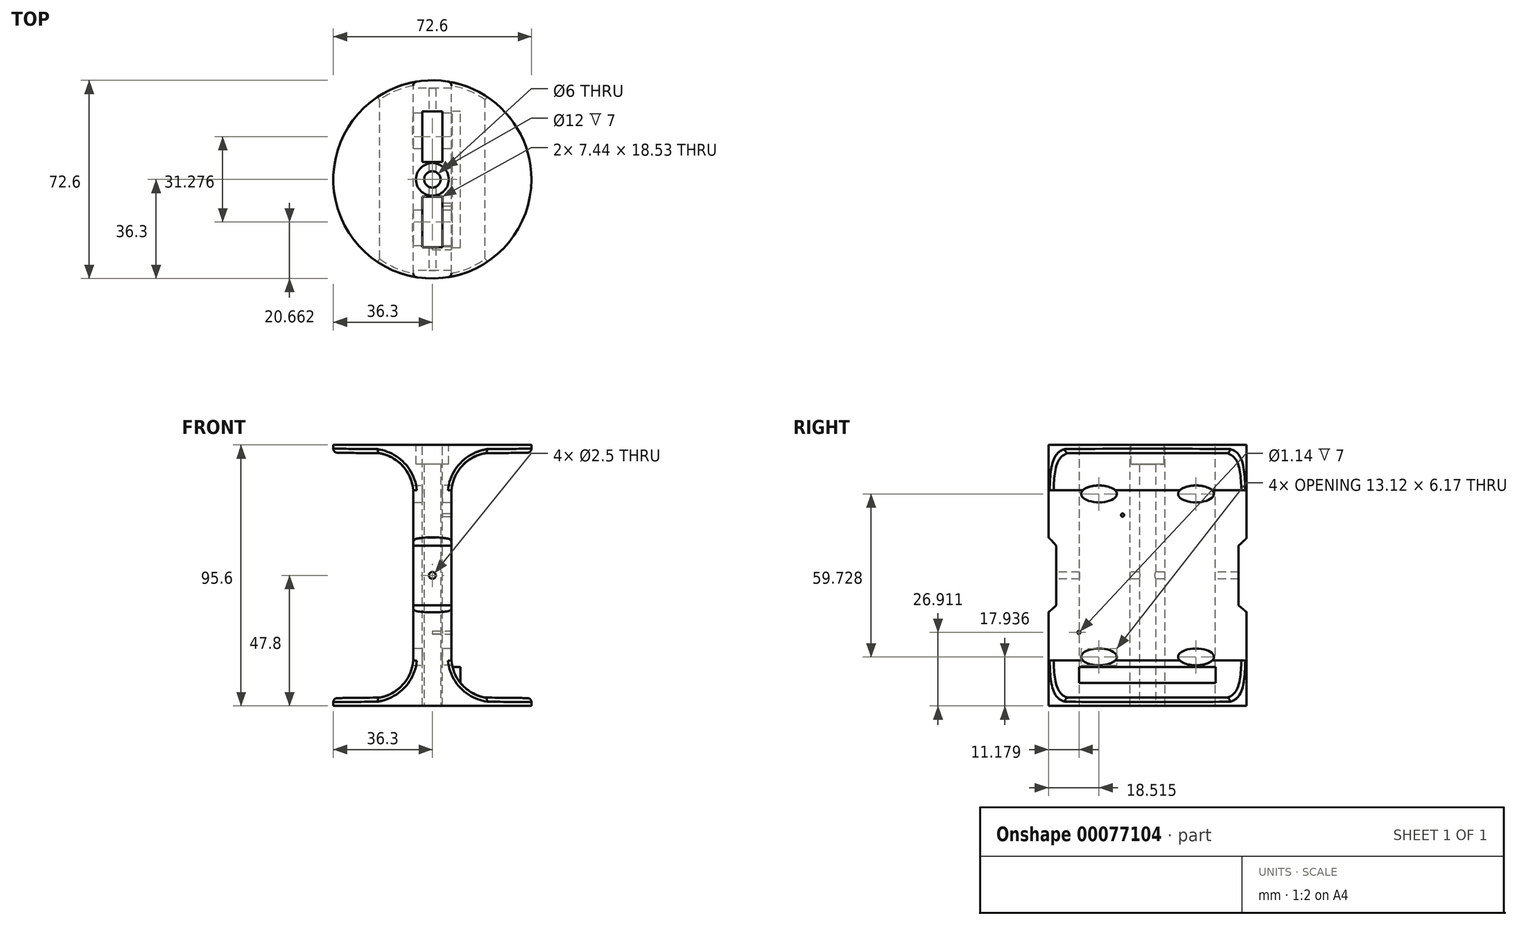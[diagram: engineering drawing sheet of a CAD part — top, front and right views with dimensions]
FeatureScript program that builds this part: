
annotation { "Feature Type Name" : "Feature", "Feature Type Description" : "" }
export const myFeature = defineFeature(function(context is Context, id is Id, definition is map)
    precondition{}
    {
        {
            var Q0;
            Q0=qCreatedBy(makeId("Top.planeOp"),FACE);
            var sketch = newSketch(context, id + "F0", { "sketchPlane" : qUnion([Q0])});
            skCircle(sketch, "E0", {"center": v(0, 0) * mm, "radius": 36.3 * mm});
            skCircle(sketch, "E1", {"center": v(0, 0) * mm, "radius": 3 * mm});
            skSolve(sketch);
        }
        {
            var Q0;
            Q0=makeQuery(id+"F0.imprint","IMPRINT",FACE,{"disambiguationData":[TD([[makeQuery(id+"F0.imprint","IMPRINT",EDGE,{"derivedFrom":sQuery(id+"F0.wireOp",EDGE,"E0")}),1.0]])]});
            extrude(context, id + "F1", {"entities" : qUnion([Q0]), "depth" : 95.6 * mm, "offsetDistance" : 25 * mm, "symmetric" : true});
        }
        {
            var Q0;
            Q0=qCreatedBy(makeId("Front.planeOp"),FACE);
            var sketch = newSketch(context, id + "F2", { "sketchPlane" : qUnion([Q0])});
            skArc(sketch, "E2", {"start": v(-7, 31.17) * mm, "mid": v(-11.47, 40.72) * mm, "end": v(-21.1, 44.98) * mm});
            skPoint(sketch, "E2.first.point", {"position": v(-26.4, 44.33) * mm});
            skPoint(sketch, "E2.second.point", {"position": v(-13.67, 17.5) * mm});
            skPoint(sketch, "E2.third.point", {"position": v(-11.88, 18.9) * mm});
            skLineSegment(sketch, "E3", {"start": v(-33.8, 39.21) * mm, "end": v(-33.85, 39.2) * mm});
            skLineSegment(sketch, "E4", {"start": v(-7, 31.17) * mm, "end": v(-7, 0) * mm});
            skLineSegment(sketch, "E5", {"start": v(-29.95, 0) * mm, "end": v(-7, 0) * mm, "construction": true});
            skLineSegment(sketch, "E6.MirrorCS", {"start": v(-7, -31.17) * mm, "end": v(-7, 0) * mm});
            skPoint(sketch, "E7.orphan", {"position": v(-22.37, 15) * mm});
            skPoint(sketch, "E8.orphan", {"position": v(-22.37, -15) * mm});
            skPoint(sketch, "E9.orphan", {"position": v(-13.67, -17.5) * mm});
            skLineSegment(sketch, "E10.MirrorCS", {"start": v(-33.8, -39.21) * mm, "end": v(-33.85, -39.2) * mm});
            skPoint(sketch, "E11.MirrorCS.end.orphan", {"position": v(-29.95, 0) * mm});
            skPoint(sketch, "E11.MirrorCS.start.orphan", {"position": v(-29.95, -17.3) * mm});
            skPoint(sketch, "E12.MirrorCS.center.orphan", {"position": v(-21.96, -30) * mm});
            skPoint(sketch, "E12.MirrorCS.end.orphan", {"position": v(-21.1, -44.98) * mm});
            skLineSegment(sketch, "E13", {"start": v(-19.34, 44.77) * mm, "end": v(-37.9, 44.98) * mm});
            skLineSegment(sketch, "E14.MirrorCS", {"start": v(-19.34, -44.77) * mm, "end": v(-37.9, -44.98) * mm});
            skArc(sketch, "E15.MirrorCS", {"start": v(-7, -31.17) * mm, "mid": v(-11.47, -40.72) * mm, "end": v(-21.1, -44.98) * mm});
            skPoint(sketch, "E16.start.orphan", {"position": v(-29.95, 17.3) * mm});
            skLineSegment(sketch, "E17", {"start": v(-37.9, 44.98) * mm, "end": v(-37.9, -44.98) * mm});
            skPoint(sketch, "E18.end.orphan", {"position": v(-36.94, 29.1) * mm});
            skPoint(sketch, "E19.MirrorCS.end.orphan", {"position": v(-36.94, -29.1) * mm});
            skPoint(sketch, "E20.MirrorCS.start.orphan", {"position": v(-33.28, -39.85) * mm});
            skPoint(sketch, "E21.MirrorCS.start.orphan", {"position": v(-33.85, -39.2) * mm});
            skPoint(sketch, "E22.end.orphan", {"position": v(-33.28, 39.85) * mm});
            skSolve(sketch);
        }
        {
            var Q0;
            {var subQ0=sQuery(id+"F2.wireOp",EDGE,"E2");Q0=makeQuery(id+"F2.imprint","IMPRINT",FACE,{"disambiguationData":[TD([[makeQuery(id+"F2.imprint","IMPRINT",EDGE,{"derivedFrom":subQ0}),1.0]])]});}
            extrude(context, id + "F3", {"entities" : qUnion([Q0]), "depth" : 100 * mm, "offsetDistance" : 25 * mm, "symmetric" : true});
        }
        {
            var Q0;
            Q0=makeQuery(id+"F3.opExtrude","SWEPT_BODY",BODY,{"disambiguationData":[OSD([sQuery(id+"F2.wireOp",EDGE,"E2"),sQuery(id+"F2.wireOp",EDGE,"2f42745c-d287-4b53-8fb5-9bfce6a12ec3"),sQuery(id+"F2.wireOp",EDGE,"bZKIiQnf-FhRn-fojp-zsQL-YmqztP06htcK")])]});
            var Q1;
            Q1=qCreatedBy(makeId("Right.planeOp"),FACE);
            mirror(context, id + "F4", {"operationType" : NewBodyOperationType.REMOVE, "entities" : qUnion([Q0]), "mirrorPlane" : qUnion([Q1])});
        }
        {
            var Q0;
            Q0=makeQuery(id+"F3.opExtrude","SWEPT_BODY",BODY,{"disambiguationData":[OSD([sQuery(id+"F2.wireOp",EDGE,"E2"),sQuery(id+"F2.wireOp",EDGE,"2f42745c-d287-4b53-8fb5-9bfce6a12ec3"),sQuery(id+"F2.wireOp",EDGE,"bZKIiQnf-FhRn-fojp-zsQL-YmqztP06htcK")])]});
            var Q1;
            Q1=makeQuery(id+"F1.opExtrude","SWEPT_BODY",BODY,{"disambiguationData":[OSD([sQuery(id+"F0.wireOp",EDGE,"E0"),sQuery(id+"F0.wireOp",EDGE,"E1")])]});
            booleanBodies(context, id + "F5", {"operationType" : BooleanOperationType.SUBTRACTION, "tools" : qUnion([Q0]), "targets" : qUnion([Q1])});
        }
        {
            var Q0;
            Q0=makeQuery(id+"F1.opExtrude","CAP_FACE",FACE,{"disambiguationData":[OSD([sQuery(id+"F0.wireOp",EDGE,"E0"),sQuery(id+"F0.wireOp",EDGE,"E1")])],"isStart":false});
            var sketch = newSketch(context, id + "F6", { "sketchPlane" : qUnion([Q0])});
            skLineSegment(sketch, "E23.bottom", {"start": v(-4.66, 24.9) * mm, "end": v(3.72, 24.9) * mm});
            skLineSegment(sketch, "E23.top", {"start": v(-4.66, 6.37) * mm, "end": v(3.72, 6.37) * mm});
            skLineSegment(sketch, "E23.left", {"start": v(-4.66, 24.9) * mm, "end": v(-4.66, 6.37) * mm});
            skLineSegment(sketch, "E23.right", {"start": v(3.72, 24.9) * mm, "end": v(3.72, 6.37) * mm});
            skLineSegment(sketch, "E24", {"start": v(0, 63.63) * mm, "end": v(0, -56.2) * mm, "construction": true});
            skLineSegment(sketch, "E25.MirrorCS", {"start": v(4.66, 24.9) * mm, "end": v(-3.72, 24.9) * mm});
            skLineSegment(sketch, "E26.MirrorCS", {"start": v(4.66, 24.9) * mm, "end": v(4.66, 6.37) * mm});
            skLineSegment(sketch, "E27.MirrorCS", {"start": v(4.66, 6.37) * mm, "end": v(-3.72, 6.37) * mm});
            skLineSegment(sketch, "E28.MirrorCS", {"start": v(-3.72, 24.9) * mm, "end": v(-3.72, 6.37) * mm});
            skSolve(sketch);
        }
        {
            var Q0;
            {var subQ0=sQuery(id+"F6.wireOp",EDGE,"E23.right");Q0=makeQuery(id+"F6.imprint","IMPRINT",FACE,{"disambiguationData":[TD([[makeQuery(id+"F6.imprint","IMPRINT",EDGE,{"derivedFrom":subQ0}),-1.0]])]});}
            var Q1;
            Q1=makeQuery(id+"F1.opExtrude","CAP_FACE",FACE,{"disambiguationData":[OSD([sQuery(id+"F0.wireOp",EDGE,"E0"),sQuery(id+"F0.wireOp",EDGE,"E1")])],"isStart":true});
            extrude(context, id + "F7", {"entities" : qUnion([Q0]), "endBound" : BoundingType.UP_TO_SURFACE, "oppositeDirection" : true, "depth" : 25 * mm, "endBoundEntityFace" : qUnion([Q1]), "offsetDistance" : 25 * mm});
        }
        {
            var Q0;
            Q0=makeQuery(id+"F7.opExtrude","SWEPT_BODY",BODY,{"disambiguationData":[OSD([sQuery(id+"F6.wireOp",EDGE,"E23.right"),sQuery(id+"F6.wireOp",EDGE,"E28.MirrorCS"),sQuery(id+"F6.wireOp",EDGE,"E23.top"),sQuery(id+"F6.wireOp",EDGE,"E23.bottom")])]});
            var Q1;
            Q1=qCreatedBy(makeId("Front.planeOp"),FACE);
            mirror(context, id + "F8", {"operationType" : NewBodyOperationType.REMOVE, "entities" : qUnion([Q0]), "mirrorPlane" : qUnion([Q1])});
        }
        {
            var Q0;
            Q0=makeQuery(id+"F7.opExtrude","SWEPT_BODY",BODY,{"disambiguationData":[OSD([sQuery(id+"F6.wireOp",EDGE,"E23.right"),sQuery(id+"F6.wireOp",EDGE,"E28.MirrorCS"),sQuery(id+"F6.wireOp",EDGE,"E23.top"),sQuery(id+"F6.wireOp",EDGE,"E23.bottom")])]});
            var Q1;
            Q1=makeQuery(id+"F1.opExtrude","SWEPT_BODY",BODY,{"disambiguationData":[OSD([sQuery(id+"F0.wireOp",EDGE,"E0"),sQuery(id+"F0.wireOp",EDGE,"E1")])]});
            booleanBodies(context, id + "F9", {"operationType" : BooleanOperationType.SUBTRACTION, "tools" : qUnion([Q0]), "targets" : qUnion([Q1])});
        }
        {
            var Q0;
            Q0=qCreatedBy(makeId("Right.planeOp"),FACE);
            var sketch = newSketch(context, id + "F10", { "sketchPlane" : qUnion([Q0])});
            skLineSegment(sketch, "E29.left", {"start": v(-41.37, 0) * mm, "end": v(-41.37, 10.94) * mm});
            skLineSegment(sketch, "E29.right", {"start": v(-33.38, 0) * mm, "end": v(-33.38, 10.94) * mm});
            skLineSegment(sketch, "E30.MirrorCS", {"start": v(-41.37, 0) * mm, "end": v(-41.37, -9.04) * mm});
            skLineSegment(sketch, "E31.MirrorCS", {"start": v(-33.38, 0) * mm, "end": v(-33.38, -9.04) * mm});
            skLineSegment(sketch, "E32.MirrorCS", {"start": v(-41.37, 0) * mm, "end": v(-41.37, -10.94) * mm});
            skLineSegment(sketch, "E33.MirrorCS", {"start": v(-33.38, 0) * mm, "end": v(-33.38, -10.94) * mm});
            skLineSegment(sketch, "E34.MirrorCS", {"start": v(33.38, 0) * mm, "end": v(33.38, 10.94) * mm});
            skLineSegment(sketch, "E35.MirrorCS", {"start": v(41.37, 0) * mm, "end": v(41.37, -10.94) * mm});
            skLineSegment(sketch, "E36.MirrorCS", {"start": v(41.37, 0) * mm, "end": v(41.37, 10.94) * mm});
            skLineSegment(sketch, "E37.MirrorCS", {"start": v(33.38, 0) * mm, "end": v(33.38, -10.94) * mm});
            skLineSegment(sketch, "E38", {"start": v(-33.38, 10.94) * mm, "end": v(-41.37, 19.28) * mm});
            skLineSegment(sketch, "E39", {"start": v(-41.37, 19.28) * mm, "end": v(-41.37, 10.94) * mm});
            skLineSegment(sketch, "E40", {"start": v(-33.38, -10.94) * mm, "end": v(-41.37, -18.03) * mm});
            skLineSegment(sketch, "E41", {"start": v(-41.37, -18.03) * mm, "end": v(-41.37, -10.94) * mm});
            skLineSegment(sketch, "E42", {"start": v(33.38, 10.94) * mm, "end": v(41.37, 18.2) * mm});
            skLineSegment(sketch, "E43", {"start": v(41.37, 18.2) * mm, "end": v(41.37, 10.94) * mm});
            skLineSegment(sketch, "E44", {"start": v(33.38, -10.94) * mm, "end": v(41.37, -17.85) * mm});
            skLineSegment(sketch, "E45", {"start": v(41.37, -17.85) * mm, "end": v(41.37, -10.94) * mm});
            skPoint(sketch, "E46.MirrorCS.start.orphan", {"position": v(41.37, -10.94) * mm});
            skSolve(sketch);
        }
        {
            var Q0;
            {var subQ4=sQuery(id+"F10.wireOp",EDGE,"E29.left");Q0=makeQuery(id+"F10.imprint","IMPRINT",FACE,{"disambiguationData":[TD([[makeQuery(id+"F10.imprint","IMPRINT",EDGE,{"derivedFrom":subQ4}),-1.0]])]});}
            var Q1;
            Q1=makeQuery(id+"F10.imprint","IMPRINT",FACE,{"disambiguationData":[TD([[makeQuery(id+"F10.imprint","IMPRINT",EDGE,{"derivedFrom":sQuery(id+"F10.wireOp",EDGE,"E34.MirrorCS")}),-1.0]])]});
            extrude(context, id + "F11", {"entities" : qUnion([Q0, Q1]), "operationType" : NewBodyOperationType.REMOVE, "depth" : 25 * mm, "offsetDistance" : 25 * mm, "symmetric" : true});
        }
        {
            var Q0;
            Q0=makeQuery(id+"F11.boolean.opBoolean","COPY",FACE,{"derivedFrom":makeQuery(id+"F11.opExtrude","SWEPT_FACE",FACE,{"disambiguationData":[OSD([sQuery(id+"F10.wireOp",EDGE,"E29.right"),sQuery(id+"F10.wireOp",EDGE,"E33.MirrorCS")])]})});
            var sketch = newSketch(context, id + "F12", { "sketchPlane" : qUnion([Q0])});
            skCircle(sketch, "E47", {"center": v(0, 0) * mm, "radius": 1.25 * mm});
            skSolve(sketch);
        }
        {
            var Q0;
            Q0=makeQuery(id+"F12.imprint","IMPRINT",FACE,{"disambiguationData":[TD([[makeQuery(id+"F12.imprint","IMPRINT",EDGE,{"derivedFrom":sQuery(id+"F12.wireOp",EDGE,"E47")}),1.0]])]});
            extrude(context, id + "F13", {"entities" : qUnion([Q0]), "operationType" : NewBodyOperationType.REMOVE, "oppositeDirection" : true, "depth" : 100 * mm, "offsetDistance" : 25 * mm});
        }
        {
            var Q0;
            Q0=makeQuery(id+"F4.boolean.opBoolean","COPY",FACE,{"derivedFrom":makeQuery(id+"F4.opPattern","COPY",FACE,{"derivedFrom":makeQuery(id+"F3.opExtrude","SWEPT_FACE",FACE,{"disambiguationData":[OSD([sQuery(id+"F2.wireOp",EDGE,"E4"),sQuery(id+"F2.wireOp",EDGE,"E6.MirrorCS")])]}),"instanceName":"1"})});
            var sketch = newSketch(context, id + "F14", { "sketchPlane" : qUnion([Q0])});
            skLineSegment(sketch, "E48.bottom", {"start": v(-26.56, 23.2) * mm, "end": v(-7.51, 23.2) * mm});
            skLineSegment(sketch, "E48.top", {"start": v(-26.56, -22.54) * mm, "end": v(-7.51, -22.54) * mm});
            skLineSegment(sketch, "E48.left", {"start": v(-26.56, 23.2) * mm, "end": v(-26.56, -22.54) * mm});
            skLineSegment(sketch, "E48.right", {"start": v(-7.51, 23.2) * mm, "end": v(-7.51, -22.54) * mm});
            skSolve(sketch);
        }
        {
            var Q0;
            Q0=qCreatedBy(makeId("Right.planeOp"),FACE);
            var sketch = newSketch(context, id + "F15", { "sketchPlane" : qUnion([Q0])});
            skEllipse(sketch, "E49", {"center": v(-17.79, 29.86) * mm, "majorRadius": 6.56 * mm, "minorRadius": 3.09 * mm, "majorAxis": v(1, 0)});
            skEllipse(sketch, "E50.MirrorC", {"center": v(-17.79, -29.86) * mm, "majorRadius": 6.56 * mm, "minorRadius": 3.09 * mm, "majorAxis": v(1, 0)});
            skEllipse(sketch, "E51.MirrorC", {"center": v(17.79, -29.86) * mm, "majorRadius": 6.56 * mm, "minorRadius": 3.09 * mm, "majorAxis": v(-1, 0)});
            skEllipse(sketch, "E52.MirrorC", {"center": v(17.79, 29.86) * mm, "majorRadius": 6.56 * mm, "minorRadius": 3.09 * mm, "majorAxis": v(-1, 0)});
            skSolve(sketch);
        }
        {
            var Q0;
            Q0=makeQuery(id+"F15.imprint","IMPRINT",FACE,{"disambiguationData":[TD([[makeQuery(id+"F15.imprint","IMPRINT",EDGE,{"derivedFrom":sQuery(id+"F15.wireOp",EDGE,"E49")}),1.0]])]});
            var Q1;
            Q1=makeQuery(id+"F15.imprint","IMPRINT",FACE,{"disambiguationData":[TD([[makeQuery(id+"F15.imprint","IMPRINT",EDGE,{"derivedFrom":sQuery(id+"F15.wireOp",EDGE,"E50.MirrorC")}),1.0]])]});
            var Q2;
            Q2=makeQuery(id+"F15.imprint","IMPRINT",FACE,{"disambiguationData":[TD([[makeQuery(id+"F15.imprint","IMPRINT",EDGE,{"derivedFrom":sQuery(id+"F15.wireOp",EDGE,"E52.MirrorC")}),1.0]])]});
            var Q3;
            Q3=makeQuery(id+"F15.imprint","IMPRINT",FACE,{"disambiguationData":[TD([[makeQuery(id+"F15.imprint","IMPRINT",EDGE,{"derivedFrom":sQuery(id+"F15.wireOp",EDGE,"E51.MirrorC")}),1.0]])]});
            extrude(context, id + "F16", {"entities" : qUnion([Q0, Q1, Q2, Q3]), "operationType" : NewBodyOperationType.REMOVE, "depth" : 30 * mm, "offsetDistance" : 25 * mm, "symmetric" : true});
        }
        {
            var Q0;
            Q0=makeQuery(id+"F14.imprint","IMPRINT",FACE,{"disambiguationData":[TD([[makeQuery(id+"F14.imprint","IMPRINT",EDGE,{"derivedFrom":sQuery(id+"F14.wireOp",EDGE,"E48.bottom")}),1.0]])]});
            var sketch = newSketch(context, id + "F17", { "sketchPlane" : qUnion([Q0])});
            skCircle(sketch, "E53", {"center": v(6.54, 23.06) * mm, "radius": 0.57 * mm});
            skCircle(sketch, "E54", {"center": v(23.04, 23.06) * mm, "radius": 0.57 * mm});
            skLineSegment(sketch, "E55", {"start": v(6.54, 23.06) * mm, "end": v(7.1, 23.06) * mm, "construction": true});
            skCircle(sketch, "E56", {"center": v(6.54, -22.66) * mm, "radius": 0.57 * mm});
            skLineSegment(sketch, "E57", {"start": v(6.54, 23.06) * mm, "end": v(6.54, 22.49) * mm, "construction": true});
            skLineSegment(sketch, "E58", {"start": v(6.54, -22.66) * mm, "end": v(7.1, -22.66) * mm, "construction": true});
            skCircle(sketch, "E59", {"center": v(23.04, -22.66) * mm, "radius": 0.57 * mm});
            skCircle(sketch, "E60", {"center": v(-25.12, 22.11) * mm, "radius": 0.57 * mm});
            skCircle(sketch, "E61", {"center": v(-9.12, 22.11) * mm, "radius": 0.57 * mm});
            skLineSegment(sketch, "E62", {"start": v(-25.12, 22.11) * mm, "end": v(-24.55, 22.11) * mm, "construction": true});
            skCircle(sketch, "E63", {"center": v(-25.12, -20.89) * mm, "radius": 0.57 * mm});
            skLineSegment(sketch, "E64", {"start": v(-25.12, -20.89) * mm, "end": v(-24.55, -20.89) * mm, "construction": true});
            skCircle(sketch, "E65", {"center": v(-8.62, -20.89) * mm, "radius": 0.57 * mm});
            skLineSegment(sketch, "E66", {"start": v(-25.12, 22.11) * mm, "end": v(-25.12, 21.54) * mm, "construction": true});
            skLineSegment(sketch, "E67", {"start": v(-9.12, 22.11) * mm, "end": v(-9.32, 21.58) * mm});
            skLineSegment(sketch, "E68.trimOffspring", {"start": v(-24.92, -20.35) * mm, "end": v(-25.12, -20.89) * mm});
            skLineSegment(sketch, "E69.trimOffspring", {"start": v(6.54, -22.1) * mm, "end": v(6.54, -60.18) * mm, "construction": true});
            skLineSegment(sketch, "E70.trimOffspring", {"start": v(22.47, 23.06) * mm, "end": v(25.23, 23.06) * mm, "construction": true});
            skLineSegment(sketch, "E71.trimOffspring", {"start": v(22.47, -22.66) * mm, "end": v(26.07, -22.66) * mm, "construction": true});
            skLineSegment(sketch, "E72.trimOffspring", {"start": v(-9.2, -20.89) * mm, "end": v(-8.05, -20.89) * mm, "construction": true});
            skLineSegment(sketch, "E73.trimOffspring", {"start": v(-25.12, -20.32) * mm, "end": v(-25.12, -23.48) * mm, "construction": true});
            skLineSegment(sketch, "E74.trimOffspring", {"start": v(-9.69, 22.11) * mm, "end": v(-8.55, 22.11) * mm, "construction": true});
            skSolve(sketch);
        }
        {
            var Q0;
            Q0=qCreatedBy(makeId("Front.planeOp"),FACE);
            var sketch = newSketch(context, id + "F18", { "sketchPlane" : qUnion([Q0])});
            skLineSegment(sketch, "E75.bottom", {"start": v(6.24, -33.56) * mm, "end": v(10.28, -33.56) * mm});
            skLineSegment(sketch, "E75.top", {"start": v(6.24, -40.66) * mm, "end": v(10.28, -40.66) * mm});
            skLineSegment(sketch, "E75.left", {"start": v(6.24, -33.56) * mm, "end": v(6.24, -40.66) * mm});
            skLineSegment(sketch, "E75.right", {"start": v(10.28, -33.56) * mm, "end": v(10.28, -40.66) * mm});
            skSolve(sketch);
        }
        {
            var Q0;
            Q0=makeQuery(id+"F18.imprint","IMPRINT",FACE,{"disambiguationData":[TD([[makeQuery(id+"F18.imprint","IMPRINT",EDGE,{"derivedFrom":sQuery(id+"F18.wireOp",EDGE,"E75.bottom")}),-1.0]])]});
            extrude(context, id + "F19", {"entities" : qUnion([Q0]), "operationType" : NewBodyOperationType.ADD, "depth" : 50 * mm, "offsetDistance" : 25 * mm, "symmetric" : true});
        }
        {
            var Q0;
            Q0=makeQuery(id+"F17.imprint","IMPRINT",FACE,{"disambiguationData":[TD([[makeQuery(id+"F17.imprint","IMPRINT",EDGE,{"derivedFrom":sQuery(id+"F17.wireOp",EDGE,"E61")}),1.0]])]});
            extrude(context, id + "F20", {"entities" : qUnion([Q0]), "operationType" : NewBodyOperationType.REMOVE, "oppositeDirection" : true, "depth" : 5 * mm, "offsetDistance" : 25 * mm});
        }
        {
            var Q0;
            Q0=makeQuery(id+"F17.imprint","IMPRINT",FACE,{"disambiguationData":[TD([[makeQuery(id+"F17.imprint","IMPRINT",EDGE,{"derivedFrom":sQuery(id+"F17.wireOp",EDGE,"E63")}),1.0]])]});
            extrude(context, id + "F21", {"entities" : qUnion([Q0]), "operationType" : NewBodyOperationType.REMOVE, "oppositeDirection" : true, "depth" : 7 * mm, "offsetDistance" : 25 * mm});
        }
        {
            var Q0;
            Q0=makeQuery(id+"F4.boolean.opBoolean","INTERSECT",EDGE,{"disambiguationData":[OD(1.0)],"derivedFrom":[makeQuery(id+"F1.opExtrude","SWEPT_FACE",FACE,{"disambiguationData":[OSD([sQuery(id+"F0.wireOp",EDGE,"E0")])]}),makeQuery(id+"F4.opPattern","COPY",FACE,{"derivedFrom":makeQuery(id+"F3.opExtrude","SWEPT_FACE",FACE,{"disambiguationData":[OSD([sQuery(id+"F2.wireOp",EDGE,"E2")])]}),"instanceName":"1"})]});
            var Q1;
            Q1=makeQuery(id+"F4.boolean.opBoolean","INTERSECT",EDGE,{"derivedFrom":[makeQuery(id+"F1.opExtrude","SWEPT_FACE",FACE,{"disambiguationData":[OSD([sQuery(id+"F0.wireOp",EDGE,"E0")])]}),makeQuery(id+"F4.opPattern","COPY",FACE,{"derivedFrom":makeQuery(id+"F3.opExtrude","SWEPT_FACE",FACE,{"disambiguationData":[OSD([sQuery(id+"F2.wireOp",EDGE,"E13")])]}),"instanceName":"1"})]});
            var Q2;
            {var subQ0=makeQuery(id+"F1.opExtrude","SWEPT_FACE",FACE,{"disambiguationData":[OSD([sQuery(id+"F0.wireOp",EDGE,"E0")])]});var subQ1=makeQuery(id+"F4.opPattern","COPY",FACE,{"derivedFrom":makeQuery(id+"F3.opExtrude","SWEPT_FACE",FACE,{"disambiguationData":[OSD([sQuery(id+"F2.wireOp",EDGE,"E4"),sQuery(id+"F2.wireOp",EDGE,"E6.MirrorCS")])]}),"instanceName":"1"});Q2=makeQuery(id+"F11.boolean.opBoolean","SPLIT",EDGE,{"disambiguationData":[TD([makeQuery(id+"F4.boolean.opBoolean","COPY",FACE,{"derivedFrom":makeQuery(id+"F4.opPattern","COPY",FACE,{"derivedFrom":makeQuery(id+"F3.opExtrude","SWEPT_FACE",FACE,{"disambiguationData":[OSD([sQuery(id+"F2.wireOp",EDGE,"E2")])]}),"instanceName":"1"})})])],"derivedFrom":makeQuery(id+"F4.boolean.opBoolean","INTERSECT",EDGE,{"disambiguationData":[OD(1.0)],"derivedFrom":[subQ0,subQ1]})});}
            var Q3;
            Q3=makeQuery(id+"F4.boolean.opBoolean","INTERSECT",EDGE,{"disambiguationData":[OD(0.0)],"derivedFrom":[makeQuery(id+"F1.opExtrude","SWEPT_FACE",FACE,{"disambiguationData":[OSD([sQuery(id+"F0.wireOp",EDGE,"E0")])]}),makeQuery(id+"F4.opPattern","COPY",FACE,{"derivedFrom":makeQuery(id+"F3.opExtrude","SWEPT_FACE",FACE,{"disambiguationData":[OSD([sQuery(id+"F2.wireOp",EDGE,"E2")])]}),"instanceName":"1"})]});
            var Q4;
            {var subQ0=makeQuery(id+"F1.opExtrude","SWEPT_FACE",FACE,{"disambiguationData":[OSD([sQuery(id+"F0.wireOp",EDGE,"E0")])]});var subQ1=makeQuery(id+"F4.opPattern","COPY",FACE,{"derivedFrom":makeQuery(id+"F3.opExtrude","SWEPT_FACE",FACE,{"disambiguationData":[OSD([sQuery(id+"F2.wireOp",EDGE,"E4"),sQuery(id+"F2.wireOp",EDGE,"E6.MirrorCS")])]}),"instanceName":"1"});Q4=makeQuery(id+"F11.boolean.opBoolean","SPLIT",EDGE,{"disambiguationData":[TD([makeQuery(id+"F4.boolean.opBoolean","COPY",FACE,{"derivedFrom":makeQuery(id+"F4.opPattern","COPY",FACE,{"derivedFrom":makeQuery(id+"F3.opExtrude","SWEPT_FACE",FACE,{"disambiguationData":[OSD([sQuery(id+"F2.wireOp",EDGE,"E2")])]}),"instanceName":"1"})})])],"derivedFrom":makeQuery(id+"F4.boolean.opBoolean","INTERSECT",EDGE,{"disambiguationData":[OD(0.0)],"derivedFrom":[subQ0,subQ1]})});}
            var Q5;
            {var subQ0=makeQuery(id+"F1.opExtrude","SWEPT_FACE",FACE,{"disambiguationData":[OSD([sQuery(id+"F0.wireOp",EDGE,"E0")])]});var subQ1=makeQuery(id+"F4.opPattern","COPY",FACE,{"derivedFrom":makeQuery(id+"F3.opExtrude","SWEPT_FACE",FACE,{"disambiguationData":[OSD([sQuery(id+"F2.wireOp",EDGE,"E4"),sQuery(id+"F2.wireOp",EDGE,"E6.MirrorCS")])]}),"instanceName":"1"});Q5=makeQuery(id+"F11.boolean.opBoolean","SPLIT",EDGE,{"disambiguationData":[TD([makeQuery(id+"F4.boolean.opBoolean","COPY",FACE,{"derivedFrom":makeQuery(id+"F4.opPattern","COPY",FACE,{"derivedFrom":makeQuery(id+"F3.opExtrude","SWEPT_FACE",FACE,{"disambiguationData":[OSD([sQuery(id+"F2.wireOp",EDGE,"E15.MirrorCS")])]}),"instanceName":"1"})})])],"derivedFrom":makeQuery(id+"F4.boolean.opBoolean","INTERSECT",EDGE,{"disambiguationData":[OD(0.0)],"derivedFrom":[subQ0,subQ1]})});}
            var Q6;
            Q6=makeQuery(id+"F4.boolean.opBoolean","INTERSECT",EDGE,{"disambiguationData":[OD(0.0)],"derivedFrom":[makeQuery(id+"F1.opExtrude","SWEPT_FACE",FACE,{"disambiguationData":[OSD([sQuery(id+"F0.wireOp",EDGE,"E0")])]}),makeQuery(id+"F4.opPattern","COPY",FACE,{"derivedFrom":makeQuery(id+"F3.opExtrude","SWEPT_FACE",FACE,{"disambiguationData":[OSD([sQuery(id+"F2.wireOp",EDGE,"E15.MirrorCS")])]}),"instanceName":"1"})]});
            var Q7;
            Q7=makeQuery(id+"F4.boolean.opBoolean","INTERSECT",EDGE,{"derivedFrom":[makeQuery(id+"F1.opExtrude","SWEPT_FACE",FACE,{"disambiguationData":[OSD([sQuery(id+"F0.wireOp",EDGE,"E0")])]}),makeQuery(id+"F4.opPattern","COPY",FACE,{"derivedFrom":makeQuery(id+"F3.opExtrude","SWEPT_FACE",FACE,{"disambiguationData":[OSD([sQuery(id+"F2.wireOp",EDGE,"E14.MirrorCS")])]}),"instanceName":"1"})]});
            var Q8;
            Q8=makeQuery(id+"F4.boolean.opBoolean","INTERSECT",EDGE,{"disambiguationData":[OD(1.0)],"derivedFrom":[makeQuery(id+"F1.opExtrude","SWEPT_FACE",FACE,{"disambiguationData":[OSD([sQuery(id+"F0.wireOp",EDGE,"E0")])]}),makeQuery(id+"F4.opPattern","COPY",FACE,{"derivedFrom":makeQuery(id+"F3.opExtrude","SWEPT_FACE",FACE,{"disambiguationData":[OSD([sQuery(id+"F2.wireOp",EDGE,"E15.MirrorCS")])]}),"instanceName":"1"})]});
            var Q9;
            {var subQ0=makeQuery(id+"F1.opExtrude","SWEPT_FACE",FACE,{"disambiguationData":[OSD([sQuery(id+"F0.wireOp",EDGE,"E0")])]});var subQ1=makeQuery(id+"F4.opPattern","COPY",FACE,{"derivedFrom":makeQuery(id+"F3.opExtrude","SWEPT_FACE",FACE,{"disambiguationData":[OSD([sQuery(id+"F2.wireOp",EDGE,"E4"),sQuery(id+"F2.wireOp",EDGE,"E6.MirrorCS")])]}),"instanceName":"1"});Q9=makeQuery(id+"F11.boolean.opBoolean","SPLIT",EDGE,{"disambiguationData":[TD([makeQuery(id+"F4.boolean.opBoolean","COPY",FACE,{"derivedFrom":makeQuery(id+"F4.opPattern","COPY",FACE,{"derivedFrom":makeQuery(id+"F3.opExtrude","SWEPT_FACE",FACE,{"disambiguationData":[OSD([sQuery(id+"F2.wireOp",EDGE,"E15.MirrorCS")])]}),"instanceName":"1"})})])],"derivedFrom":makeQuery(id+"F4.boolean.opBoolean","INTERSECT",EDGE,{"disambiguationData":[OD(1.0)],"derivedFrom":[subQ0,subQ1]})});}
            var Q10;
            Q10=makeQuery(id+"F5.opBoolean","INTERSECT",EDGE,{"disambiguationData":[OD(1.0)],"derivedFrom":[makeQuery(id+"F3.opExtrude","SWEPT_FACE",FACE,{"disambiguationData":[OSD([sQuery(id+"F2.wireOp",EDGE,"E15.MirrorCS")])]}),makeQuery(id+"F1.opExtrude","SWEPT_FACE",FACE,{"disambiguationData":[OSD([sQuery(id+"F0.wireOp",EDGE,"E0")])]})]});
            var Q11;
            Q11=makeQuery(id+"F5.opBoolean","INTERSECT",EDGE,{"derivedFrom":[makeQuery(id+"F3.opExtrude","SWEPT_FACE",FACE,{"disambiguationData":[OSD([sQuery(id+"F2.wireOp",EDGE,"E14.MirrorCS")])]}),makeQuery(id+"F1.opExtrude","SWEPT_FACE",FACE,{"disambiguationData":[OSD([sQuery(id+"F0.wireOp",EDGE,"E0")])]})]});
            var Q12;
            {var subQ0=makeQuery(id+"F1.opExtrude","SWEPT_FACE",FACE,{"disambiguationData":[OSD([sQuery(id+"F0.wireOp",EDGE,"E0")])]});var subQ1=makeQuery(id+"F3.opExtrude","SWEPT_FACE",FACE,{"disambiguationData":[OSD([sQuery(id+"F2.wireOp",EDGE,"E4"),sQuery(id+"F2.wireOp",EDGE,"E6.MirrorCS")])]});Q12=makeQuery(id+"F11.boolean.opBoolean","SPLIT",EDGE,{"disambiguationData":[TD([makeQuery(id+"F5.opBoolean","COPY",FACE,{"derivedFrom":makeQuery(id+"F3.opExtrude","SWEPT_FACE",FACE,{"disambiguationData":[OSD([sQuery(id+"F2.wireOp",EDGE,"E15.MirrorCS")])]})})])],"derivedFrom":makeQuery(id+"F5.opBoolean","INTERSECT",EDGE,{"disambiguationData":[OD(1.0)],"derivedFrom":[subQ1,subQ0]})});}
            var Q13;
            Q13=makeQuery(id+"F5.opBoolean","INTERSECT",EDGE,{"disambiguationData":[OD(0.0)],"derivedFrom":[makeQuery(id+"F3.opExtrude","SWEPT_FACE",FACE,{"disambiguationData":[OSD([sQuery(id+"F2.wireOp",EDGE,"E15.MirrorCS")])]}),makeQuery(id+"F1.opExtrude","SWEPT_FACE",FACE,{"disambiguationData":[OSD([sQuery(id+"F0.wireOp",EDGE,"E0")])]})]});
            var Q14;
            {var subQ0=makeQuery(id+"F1.opExtrude","SWEPT_FACE",FACE,{"disambiguationData":[OSD([sQuery(id+"F0.wireOp",EDGE,"E0")])]});var subQ1=makeQuery(id+"F3.opExtrude","SWEPT_FACE",FACE,{"disambiguationData":[OSD([sQuery(id+"F2.wireOp",EDGE,"E4"),sQuery(id+"F2.wireOp",EDGE,"E6.MirrorCS")])]});Q14=makeQuery(id+"F11.boolean.opBoolean","SPLIT",EDGE,{"disambiguationData":[TD([makeQuery(id+"F5.opBoolean","COPY",FACE,{"derivedFrom":makeQuery(id+"F3.opExtrude","SWEPT_FACE",FACE,{"disambiguationData":[OSD([sQuery(id+"F2.wireOp",EDGE,"E15.MirrorCS")])]})})])],"derivedFrom":makeQuery(id+"F5.opBoolean","INTERSECT",EDGE,{"disambiguationData":[OD(0.0)],"derivedFrom":[subQ1,subQ0]})});}
            var Q15;
            {var subQ0=makeQuery(id+"F1.opExtrude","SWEPT_FACE",FACE,{"disambiguationData":[OSD([sQuery(id+"F0.wireOp",EDGE,"E0")])]});var subQ1=makeQuery(id+"F3.opExtrude","SWEPT_FACE",FACE,{"disambiguationData":[OSD([sQuery(id+"F2.wireOp",EDGE,"E4"),sQuery(id+"F2.wireOp",EDGE,"E6.MirrorCS")])]});Q15=makeQuery(id+"F11.boolean.opBoolean","SPLIT",EDGE,{"disambiguationData":[TD([makeQuery(id+"F5.opBoolean","COPY",FACE,{"derivedFrom":makeQuery(id+"F3.opExtrude","SWEPT_FACE",FACE,{"disambiguationData":[OSD([sQuery(id+"F2.wireOp",EDGE,"E2")])]})})])],"derivedFrom":makeQuery(id+"F5.opBoolean","INTERSECT",EDGE,{"disambiguationData":[OD(0.0)],"derivedFrom":[subQ1,subQ0]})});}
            var Q16;
            Q16=makeQuery(id+"F5.opBoolean","INTERSECT",EDGE,{"disambiguationData":[OD(0.0)],"derivedFrom":[makeQuery(id+"F3.opExtrude","SWEPT_FACE",FACE,{"disambiguationData":[OSD([sQuery(id+"F2.wireOp",EDGE,"E2")])]}),makeQuery(id+"F1.opExtrude","SWEPT_FACE",FACE,{"disambiguationData":[OSD([sQuery(id+"F0.wireOp",EDGE,"E0")])]})]});
            var Q17;
            Q17=makeQuery(id+"F5.opBoolean","INTERSECT",EDGE,{"derivedFrom":[makeQuery(id+"F3.opExtrude","SWEPT_FACE",FACE,{"disambiguationData":[OSD([sQuery(id+"F2.wireOp",EDGE,"E13")])]}),makeQuery(id+"F1.opExtrude","SWEPT_FACE",FACE,{"disambiguationData":[OSD([sQuery(id+"F0.wireOp",EDGE,"E0")])]})]});
            var Q18;
            Q18=makeQuery(id+"F5.opBoolean","INTERSECT",EDGE,{"disambiguationData":[OD(1.0)],"derivedFrom":[makeQuery(id+"F3.opExtrude","SWEPT_FACE",FACE,{"disambiguationData":[OSD([sQuery(id+"F2.wireOp",EDGE,"E2")])]}),makeQuery(id+"F1.opExtrude","SWEPT_FACE",FACE,{"disambiguationData":[OSD([sQuery(id+"F0.wireOp",EDGE,"E0")])]})]});
            var Q19;
            {var subQ0=makeQuery(id+"F1.opExtrude","SWEPT_FACE",FACE,{"disambiguationData":[OSD([sQuery(id+"F0.wireOp",EDGE,"E0")])]});var subQ1=makeQuery(id+"F3.opExtrude","SWEPT_FACE",FACE,{"disambiguationData":[OSD([sQuery(id+"F2.wireOp",EDGE,"E4"),sQuery(id+"F2.wireOp",EDGE,"E6.MirrorCS")])]});Q19=makeQuery(id+"F11.boolean.opBoolean","SPLIT",EDGE,{"disambiguationData":[TD([makeQuery(id+"F5.opBoolean","COPY",FACE,{"derivedFrom":makeQuery(id+"F3.opExtrude","SWEPT_FACE",FACE,{"disambiguationData":[OSD([sQuery(id+"F2.wireOp",EDGE,"E2")])]})})])],"derivedFrom":makeQuery(id+"F5.opBoolean","INTERSECT",EDGE,{"disambiguationData":[OD(1.0)],"derivedFrom":[subQ1,subQ0]})});}
            fillet(context, id + "F22", {"entities" : qUnion([Q0, Q1, Q2, Q3, Q4, Q5, Q6, Q7, Q8, Q9, Q10, Q11, Q12, Q13, Q14, Q15, Q16, Q17, Q18, Q19]), "radius" : 1.5 * mm, "tangentPropagation" : true, "allowEdgeOverflow" : false});
        }
        {
            var Q0;
            Q0=makeQuery(id+"F1.opExtrude","CAP_FACE",FACE,{"disambiguationData":[OSD([sQuery(id+"F0.wireOp",EDGE,"E0"),sQuery(id+"F0.wireOp",EDGE,"E1")])],"isStart":false});
            var sketch = newSketch(context, id + "F23", { "sketchPlane" : qUnion([Q0])});
            skCircle(sketch, "E76", {"center": v(0, 0) * mm, "radius": 6 * mm});
            skSolve(sketch);
        }
        {
            var Q0;
            Q0=makeQuery(id+"F23.imprint","IMPRINT",FACE,{"disambiguationData":[TD([[makeQuery(id+"F23.imprint","IMPRINT",EDGE,{"derivedFrom":makeQuery(id+"F1.opExtrude","CAP_EDGE",EDGE,{"disambiguationData":[OSD([sQuery(id+"F0.wireOp",EDGE,"E1")])],"isStart":false})}),-1.0]])]});
            extrude(context, id + "F24", {"entities" : qUnion([Q0]), "operationType" : NewBodyOperationType.REMOVE, "oppositeDirection" : true, "depth" : 7 * mm, "offsetDistance" : 25 * mm});
        }
    });
